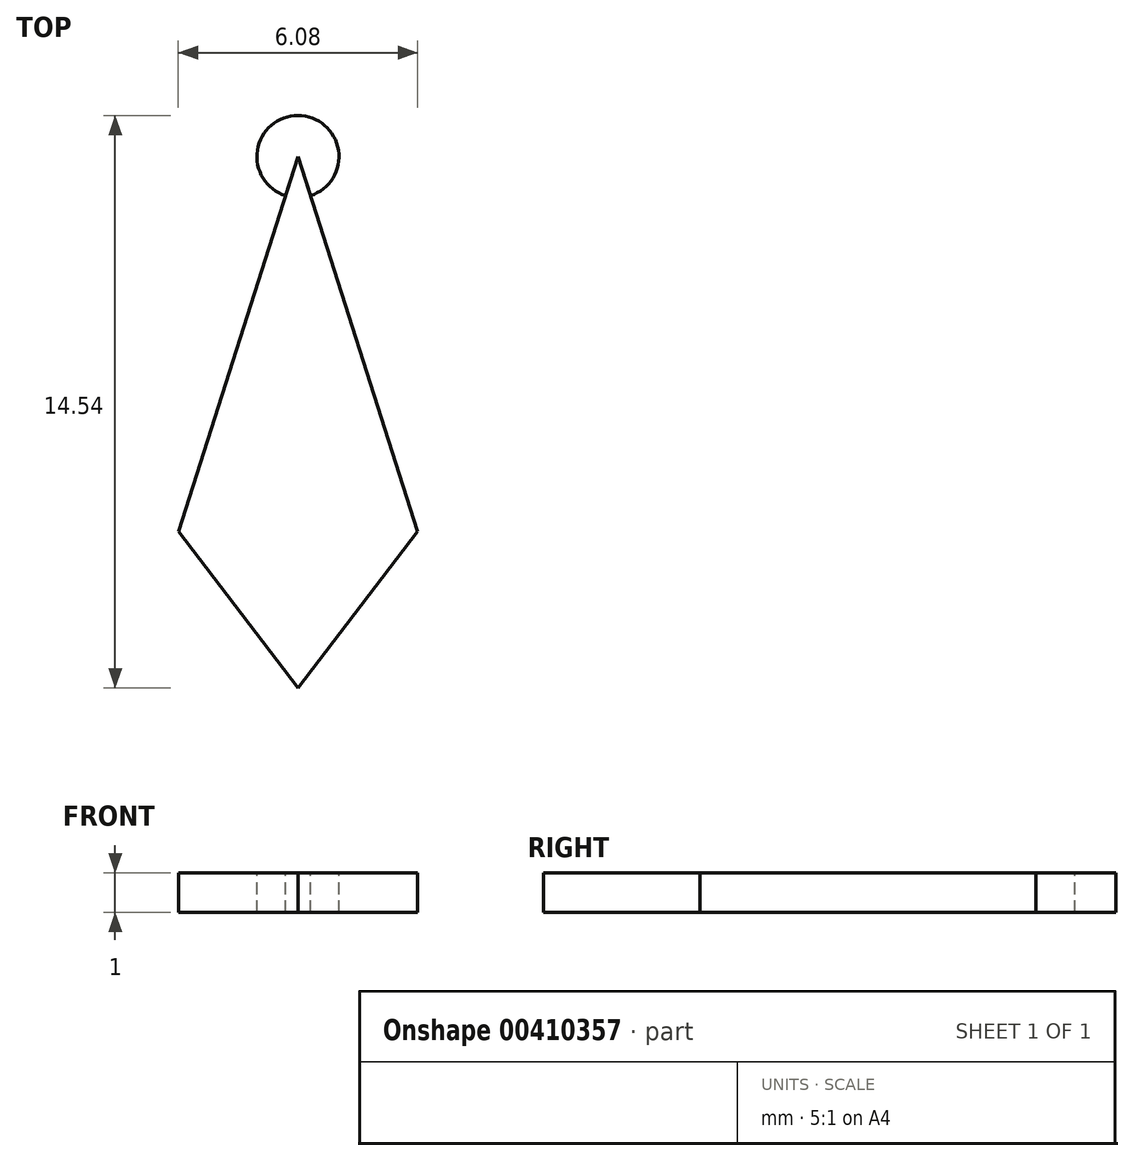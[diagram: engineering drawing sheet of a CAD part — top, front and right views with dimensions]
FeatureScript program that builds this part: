
annotation { "Feature Type Name" : "Feature", "Feature Type Description" : "" }
export const myFeature = defineFeature(function(context is Context, id is Id, definition is map)
    precondition{}
    {
        {
            var Q0;
            Q0=qCreatedBy(makeId("Top.planeOp"),FACE);
            var sketch = newSketch(context, id + "F0", { "sketchPlane" : qUnion([Q0])});
            skLineSegment(sketch, "E0", {"start": v(0, 0) * mm, "end": v(0, -13.5) * mm});
            skLineSegment(sketch, "E1", {"start": v(0, -13.5) * mm, "end": v(3.04, -9.53) * mm});
            skLineSegment(sketch, "E2", {"start": v(3.04, -9.53) * mm, "end": v(0, 0) * mm});
            skLineSegment(sketch, "E3", {"start": v(0, 0) * mm, "end": v(-3.04, -9.53) * mm});
            skLineSegment(sketch, "E4", {"start": v(-3.04, -9.53) * mm, "end": v(0, -13.5) * mm});
            skCircle(sketch, "E5", {"center": v(0, 0) * mm, "radius": 2.5 * mm});
            skSolve(sketch);
        }
        {
            var Q0;
            {var subQ3=sQuery(id+"F0.wireOp",EDGE,"E4");Q0=makeQuery(id+"F0.imprint","IMPRINT",FACE,{"disambiguationData":[TD([[makeQuery(id+"F0.imprint","IMPRINT",EDGE,{"derivedFrom":subQ3}),1.0]])]});}
            var Q1;
            {var subQ3=sQuery(id+"F0.wireOp",EDGE,"E1");Q1=makeQuery(id+"F0.imprint","IMPRINT",FACE,{"disambiguationData":[TD([[makeQuery(id+"F0.imprint","IMPRINT",EDGE,{"derivedFrom":subQ3}),1.0]])]});}
            var Q2;
            {var subQ0=sQuery(id+"F0.wireOp",EDGE,"E5");var subQ1=sQuery(id+"F0.wireOp",EDGE,"E0");var subQ2=makeQuery(id+"F0.imprint","INTERSECT",VERTEX,{"derivedFrom":[subQ1,subQ0]});Q2=makeQuery(id+"F0.imprint","IMPRINT",FACE,{"disambiguationData":[TD([[makeQuery(id+"F0.imprint","IMPRINT",EDGE,{"disambiguationData":[TD([[subQ2,1.0]])],"derivedFrom":subQ1}),-1.0]])]});}
            var Q3;
            {var subQ0=sQuery(id+"F0.wireOp",EDGE,"E5");var subQ1=sQuery(id+"F0.wireOp",EDGE,"E0");var subQ2=makeQuery(id+"F0.imprint","INTERSECT",VERTEX,{"derivedFrom":[subQ1,subQ0]});Q3=makeQuery(id+"F0.imprint","IMPRINT",FACE,{"disambiguationData":[TD([[makeQuery(id+"F0.imprint","IMPRINT",EDGE,{"disambiguationData":[TD([[subQ2,1.0]])],"derivedFrom":subQ1}),1.0]])]});}
            extrude(context, id + "F1", {"entities" : qUnion([Q0, Q1, Q2, Q3]), "depth" : 1 * mm, "offsetDistance" : 25 * mm});
        }
        {
            var Q0;
            Q0=makeQuery(id+"F1.opExtrude","CAP_FACE",FACE,{"disambiguationData":[OSD([sQuery(id+"F0.wireOp",EDGE,"E1"),sQuery(id+"F0.wireOp",EDGE,"E2"),sQuery(id+"F0.wireOp",EDGE,"E3"),sQuery(id+"F0.wireOp",EDGE,"E4")])],"isStart":false});
            var sketch = newSketch(context, id + "F2", { "sketchPlane" : qUnion([Q0])});
            skCircle(sketch, "E6", {"center": v(0, 0) * mm, "radius": 1.04 * mm});
            skSolve(sketch);
        }
        {
            var Q0;
            {var subQ0=sQuery(id+"F2.wireOp",EDGE,"E6");var subQ1=makeQuery(id+"F1.opExtrude","CAP_EDGE",EDGE,{"disambiguationData":[OSD([sQuery(id+"F0.wireOp",EDGE,"E2")])],"isStart":false});var subQ2=makeQuery(id+"F2.imprint","INTERSECT",VERTEX,{"derivedFrom":[subQ1,subQ0]});Q0=makeQuery(id+"F2.imprint","IMPRINT",FACE,{"disambiguationData":[TD([[makeQuery(id+"F2.imprint","IMPRINT",EDGE,{"disambiguationData":[TD([[subQ2,-1.0]])],"derivedFrom":subQ0}),1.0]])]});}
            extrude(context, id + "F3", {"entities" : qUnion([Q0]), "oppositeDirection" : true, "depth" : 1 * mm, "offsetDistance" : 25 * mm});
        }
    });
